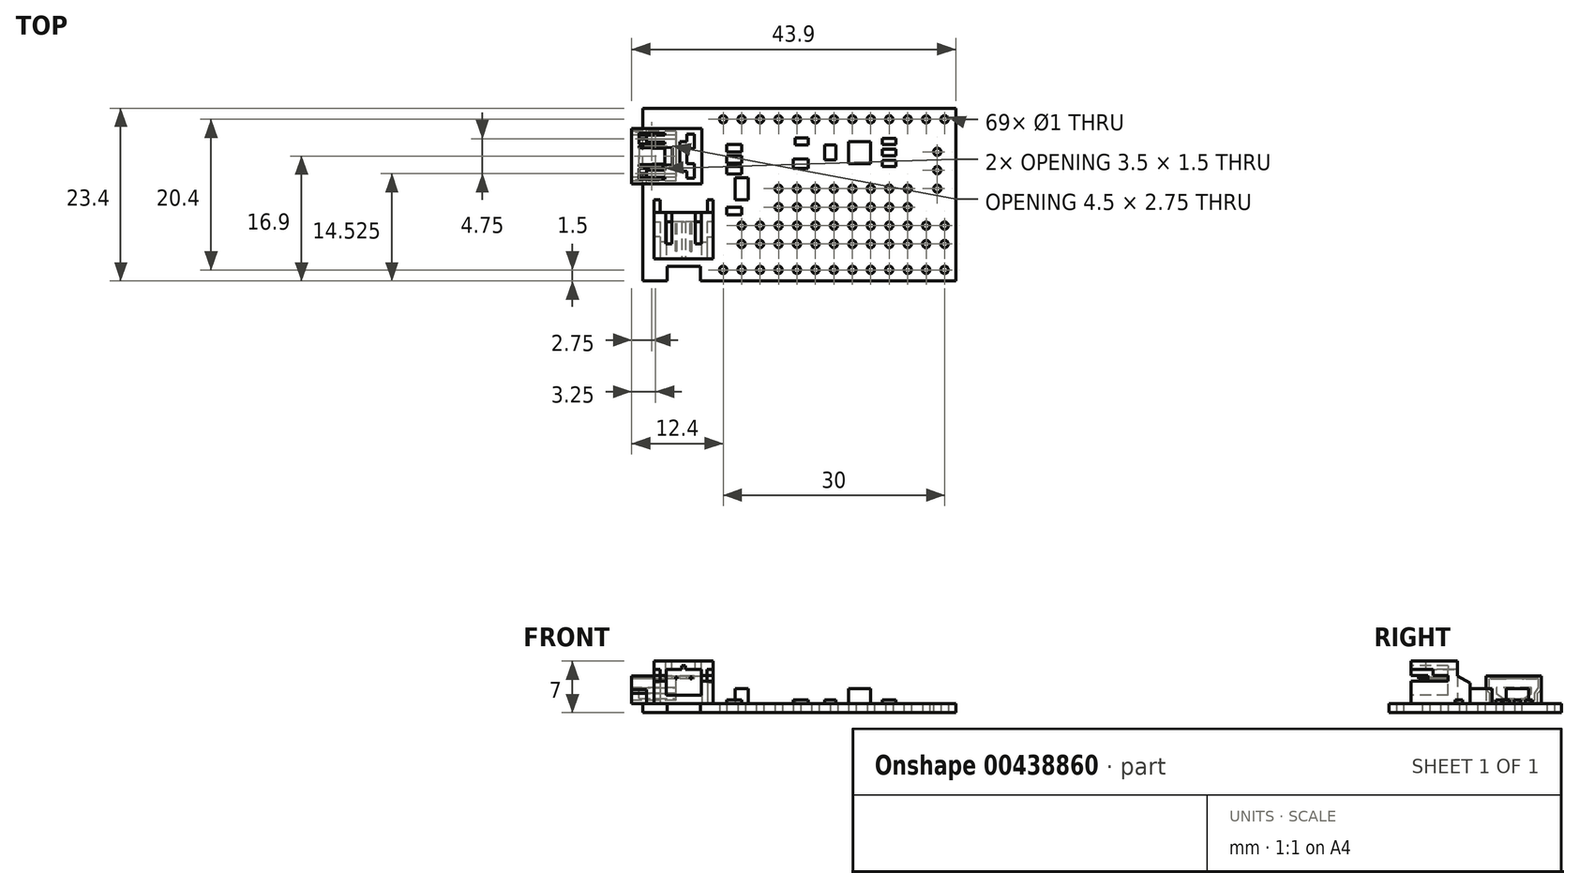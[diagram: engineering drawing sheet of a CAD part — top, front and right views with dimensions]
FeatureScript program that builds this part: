
annotation { "Feature Type Name" : "Feature", "Feature Type Description" : "" }
export const myFeature = defineFeature(function(context is Context, id is Id, definition is map)
    precondition{}
    {
        {
            var Q0;
            Q0=qCreatedBy(makeId("Top.planeOp"),FACE);
            var sketch = newSketch(context, id + "F0", { "sketchPlane" : qUnion([Q0])});
            skLineSegment(sketch, "E0.bottom", {"start": v(21.2, -11.7) * mm, "end": v(-21.2, -11.7) * mm});
            skLineSegment(sketch, "E0.top", {"start": v(21.2, 11.7) * mm, "end": v(-21.2, 11.7) * mm});
            skLineSegment(sketch, "E0.left", {"start": v(21.2, -11.7) * mm, "end": v(21.2, 11.7) * mm});
            skLineSegment(sketch, "E0.right", {"start": v(-21.2, -11.7) * mm, "end": v(-21.2, 11.7) * mm});
            skPoint(sketch, "E0.middle", {"position": v(0, 0) * mm});
            skLineSegment(sketch, "E1.bottom", {"start": v(-17.9, -11.7) * mm, "end": v(-13.4, -11.7) * mm, "construction": true});
            skLineSegment(sketch, "E1.top", {"start": v(-17.9, -9.7) * mm, "end": v(-13.4, -9.7) * mm});
            skLineSegment(sketch, "E1.left", {"start": v(-17.9, -11.7) * mm, "end": v(-17.9, -9.7) * mm});
            skLineSegment(sketch, "E1.right", {"start": v(-13.4, -11.7) * mm, "end": v(-13.4, -9.7) * mm});
            skCircle(sketch, "E2", {"center": v(19.7, -10.2) * mm, "radius": 0.5 * mm});
            skCircle(sketch, "E3.1.0.0", {"center": v(17.2, -10.2) * mm, "radius": 0.5 * mm});
            skCircle(sketch, "E3.2.0.0", {"center": v(14.7, -10.2) * mm, "radius": 0.5 * mm});
            skCircle(sketch, "E3.3.0.0", {"center": v(12.2, -10.2) * mm, "radius": 0.5 * mm});
            skCircle(sketch, "E3.4.0.0", {"center": v(9.7, -10.2) * mm, "radius": 0.5 * mm});
            skCircle(sketch, "E3.5.0.0", {"center": v(7.2, -10.2) * mm, "radius": 0.5 * mm});
            skCircle(sketch, "E3.6.0.0", {"center": v(4.7, -10.2) * mm, "radius": 0.5 * mm});
            skCircle(sketch, "E3.7.0.0", {"center": v(2.2, -10.2) * mm, "radius": 0.5 * mm});
            skCircle(sketch, "E3.8.0.0", {"center": v(-0.3, -10.2) * mm, "radius": 0.5 * mm});
            skCircle(sketch, "E3.9.0.0", {"center": v(-2.8, -10.2) * mm, "radius": 0.5 * mm});
            skCircle(sketch, "E3.10.0.0", {"center": v(-5.3, -10.2) * mm, "radius": 0.5 * mm});
            skCircle(sketch, "E3.11.0.0", {"center": v(-7.8, -10.2) * mm, "radius": 0.5 * mm});
            skCircle(sketch, "E3.12.0.0", {"center": v(-10.3, -10.2) * mm, "radius": 0.5 * mm});
            skLineSegment(sketch, "E3.direction1", {"start": v(19.7, -10.2) * mm, "end": v(17.2, -10.2) * mm, "construction": true});
            skCircle(sketch, "E4.0.1.0", {"center": v(-5.3, -6.7) * mm, "radius": 0.5 * mm});
            skCircle(sketch, "E4.0.1.1", {"center": v(-0.3, -6.7) * mm, "radius": 0.5 * mm});
            skCircle(sketch, "E4.0.1.2", {"center": v(17.2, -6.7) * mm, "radius": 0.5 * mm});
            skCircle(sketch, "E4.0.1.3", {"center": v(14.7, -6.7) * mm, "radius": 0.5 * mm});
            skCircle(sketch, "E4.0.1.4", {"center": v(12.2, -6.7) * mm, "radius": 0.5 * mm});
            skCircle(sketch, "E4.0.1.5", {"center": v(9.7, -6.7) * mm, "radius": 0.5 * mm});
            skCircle(sketch, "E4.0.1.6", {"center": v(19.7, -6.7) * mm, "radius": 0.5 * mm});
            skCircle(sketch, "E4.0.1.7", {"center": v(2.2, -6.7) * mm, "radius": 0.5 * mm});
            skCircle(sketch, "E4.0.1.8", {"center": v(4.7, -6.7) * mm, "radius": 0.5 * mm});
            skCircle(sketch, "E4.0.1.9", {"center": v(7.2, -6.7) * mm, "radius": 0.5 * mm});
            skCircle(sketch, "E4.0.1.10", {"center": v(-2.8, -6.7) * mm, "radius": 0.5 * mm});
            skCircle(sketch, "E4.0.1.12", {"center": v(-7.8, -6.7) * mm, "radius": 0.5 * mm});
            skLineSegment(sketch, "E4.direction1", {"start": v(-7.8, -10.2) * mm, "end": v(17.6, -10.2) * mm, "construction": true});
            skLineSegment(sketch, "E4.direction2", {"start": v(-7.8, -10.2) * mm, "end": v(-7.8, -6.7) * mm, "construction": true});
            skLineSegment(sketch, "E5.direction1", {"start": v(-7.8, -6.7) * mm, "end": v(17.6, -6.7) * mm, "construction": true});
            skLineSegment(sketch, "E5.direction2", {"start": v(-7.8, -6.7) * mm, "end": v(-7.8, -4.85) * mm, "construction": true});
            skPoint(sketch, "E6", {"position": v(-7.8, -8.45) * mm});
            skCircle(sketch, "E7.0.1.0", {"center": v(2.2, -4.2) * mm, "radius": 0.5 * mm});
            skCircle(sketch, "E7.0.1.1", {"center": v(9.7, -4.2) * mm, "radius": 0.5 * mm});
            skCircle(sketch, "E7.0.1.2", {"center": v(-5.3, -4.2) * mm, "radius": 0.5 * mm});
            skCircle(sketch, "E7.0.1.3", {"center": v(17.2, -4.2) * mm, "radius": 0.5 * mm});
            skCircle(sketch, "E7.0.1.4", {"center": v(-2.8, -4.2) * mm, "radius": 0.5 * mm});
            skCircle(sketch, "E7.0.1.5", {"center": v(-0.3, -4.2) * mm, "radius": 0.5 * mm});
            skCircle(sketch, "E7.0.1.6", {"center": v(14.7, -4.2) * mm, "radius": 0.5 * mm});
            skCircle(sketch, "E7.0.1.7", {"center": v(4.7, -4.2) * mm, "radius": 0.5 * mm});
            skCircle(sketch, "E7.0.1.8", {"center": v(7.2, -4.2) * mm, "radius": 0.5 * mm});
            skCircle(sketch, "E7.0.1.10", {"center": v(12.2, -4.2) * mm, "radius": 0.5 * mm});
            skCircle(sketch, "E7.0.1.11", {"center": v(19.7, -4.2) * mm, "radius": 0.5 * mm});
            skCircle(sketch, "E7.0.1.12", {"center": v(-7.8, -4.2) * mm, "radius": 0.5 * mm});
            skCircle(sketch, "E7.0.2.0", {"center": v(2.2, -1.7) * mm, "radius": 0.5 * mm});
            skCircle(sketch, "E7.0.2.1", {"center": v(9.7, -1.7) * mm, "radius": 0.5 * mm});
            skCircle(sketch, "E7.0.2.4", {"center": v(-2.8, -1.7) * mm, "radius": 0.5 * mm});
            skCircle(sketch, "E7.0.2.5", {"center": v(-0.3, -1.7) * mm, "radius": 0.5 * mm});
            skCircle(sketch, "E7.0.2.6", {"center": v(14.7, -1.7) * mm, "radius": 0.5 * mm});
            skCircle(sketch, "E7.0.2.7", {"center": v(4.7, -1.7) * mm, "radius": 0.5 * mm});
            skCircle(sketch, "E7.0.2.8", {"center": v(7.2, -1.7) * mm, "radius": 0.5 * mm});
            skCircle(sketch, "E7.0.2.10", {"center": v(12.2, -1.7) * mm, "radius": 0.5 * mm});
            skCircle(sketch, "E7.0.3.0", {"center": v(2.2, 0.8) * mm, "radius": 0.5 * mm});
            skCircle(sketch, "E7.0.3.1", {"center": v(9.7, 0.8) * mm, "radius": 0.5 * mm});
            skCircle(sketch, "E7.0.3.4", {"center": v(-2.8, 0.8) * mm, "radius": 0.5 * mm});
            skCircle(sketch, "E7.0.3.5", {"center": v(-0.3, 0.8) * mm, "radius": 0.5 * mm});
            skCircle(sketch, "E7.0.3.6", {"center": v(14.7, 0.8) * mm, "radius": 0.5 * mm});
            skCircle(sketch, "E7.0.3.7", {"center": v(4.7, 0.8) * mm, "radius": 0.5 * mm});
            skCircle(sketch, "E7.0.3.8", {"center": v(7.2, 0.8) * mm, "radius": 0.5 * mm});
            skCircle(sketch, "E7.0.3.10", {"center": v(12.2, 0.8) * mm, "radius": 0.5 * mm});
            skLineSegment(sketch, "E7.direction2", {"start": v(-7.8, -6.7) * mm, "end": v(-7.8, -4.2) * mm, "construction": true});
            skCircle(sketch, "E8", {"center": v(19.7, 10.2) * mm, "radius": 0.5 * mm});
            skCircle(sketch, "E9.1.0.0", {"center": v(17.2, 10.2) * mm, "radius": 0.5 * mm});
            skCircle(sketch, "E9.2.0.0", {"center": v(14.7, 10.2) * mm, "radius": 0.5 * mm});
            skCircle(sketch, "E9.3.0.0", {"center": v(12.2, 10.2) * mm, "radius": 0.5 * mm});
            skCircle(sketch, "E9.4.0.0", {"center": v(9.7, 10.2) * mm, "radius": 0.5 * mm});
            skCircle(sketch, "E9.5.0.0", {"center": v(7.2, 10.2) * mm, "radius": 0.5 * mm});
            skCircle(sketch, "E9.6.0.0", {"center": v(4.7, 10.2) * mm, "radius": 0.5 * mm});
            skCircle(sketch, "E9.7.0.0", {"center": v(2.2, 10.2) * mm, "radius": 0.5 * mm});
            skCircle(sketch, "E9.8.0.0", {"center": v(-0.3, 10.2) * mm, "radius": 0.5 * mm});
            skCircle(sketch, "E9.9.0.0", {"center": v(-2.8, 10.2) * mm, "radius": 0.5 * mm});
            skCircle(sketch, "E9.10.0.0", {"center": v(-5.3, 10.2) * mm, "radius": 0.5 * mm});
            skCircle(sketch, "E9.11.0.0", {"center": v(-7.8, 10.2) * mm, "radius": 0.5 * mm});
            skCircle(sketch, "E9.12.0.0", {"center": v(-10.3, 10.2) * mm, "radius": 0.5 * mm});
            skLineSegment(sketch, "E9.direction1", {"start": v(19.7, 10.2) * mm, "end": v(17.2, 10.2) * mm, "construction": true});
            skCircle(sketch, "E10", {"center": v(18.7, 0.8) * mm, "radius": 0.5 * mm});
            skCircle(sketch, "E11.0.1.0", {"center": v(18.7, 3.3) * mm, "radius": 0.5 * mm});
            skCircle(sketch, "E11.0.2.0", {"center": v(18.7, 5.8) * mm, "radius": 0.5 * mm});
            skLineSegment(sketch, "E11.direction1", {"start": v(18.7, 0.8) * mm, "end": v(43.86, 0.8) * mm, "construction": true});
            skLineSegment(sketch, "E11.direction2", {"start": v(18.7, 0.8) * mm, "end": v(18.7, 3.3) * mm, "construction": true});
            skSolve(sketch);
        }
        {
            var Q0;
            Q0=makeQuery(id+"F0.imprint","IMPRINT",FACE,{"disambiguationData":[TD([[makeQuery(id+"F0.imprint","IMPRINT",EDGE,{"derivedFrom":sQuery(id+"F0.wireOp",EDGE,"E0.top")}),1.0]])]});
            extrude(context, id + "F1", {"entities" : qUnion([Q0]), "depth" : 1.25 * mm});
        }
        {
            var Q0;
            Q0=makeQuery(id+"F1.opExtrude","CAP_FACE",FACE,{"disambiguationData":[OSD([sQuery(id+"F0.wireOp",EDGE,"E0.bottom"),sQuery(id+"F0.wireOp",EDGE,"E0.top"),sQuery(id+"F0.wireOp",EDGE,"E0.left"),sQuery(id+"F0.wireOp",EDGE,"E0.right"),sQuery(id+"F0.wireOp",EDGE,"E1.top"),sQuery(id+"F0.wireOp",EDGE,"E1.left"),sQuery(id+"F0.wireOp",EDGE,"E1.right"),sQuery(id+"F0.wireOp",EDGE,"E2"),sQuery(id+"F0.wireOp",EDGE,"E3.1.0.0"),sQuery(id+"F0.wireOp",EDGE,"E3.2.0.0"),sQuery(id+"F0.wireOp",EDGE,"E3.3.0.0"),sQuery(id+"F0.wireOp",EDGE,"E3.4.0.0"),sQuery(id+"F0.wireOp",EDGE,"E3.5.0.0"),sQuery(id+"F0.wireOp",EDGE,"E3.6.0.0"),sQuery(id+"F0.wireOp",EDGE,"E3.7.0.0"),sQuery(id+"F0.wireOp",EDGE,"E3.8.0.0"),sQuery(id+"F0.wireOp",EDGE,"E3.9.0.0"),sQuery(id+"F0.wireOp",EDGE,"E3.10.0.0"),sQuery(id+"F0.wireOp",EDGE,"E3.11.0.0"),sQuery(id+"F0.wireOp",EDGE,"E3.12.0.0"),sQuery(id+"F0.wireOp",EDGE,"E4.0.1.0"),sQuery(id+"F0.wireOp",EDGE,"E4.0.1.1"),sQuery(id+"F0.wireOp",EDGE,"E4.0.1.2"),sQuery(id+"F0.wireOp",EDGE,"E4.0.1.3"),sQuery(id+"F0.wireOp",EDGE,"E4.0.1.4"),sQuery(id+"F0.wireOp",EDGE,"E4.0.1.5"),sQuery(id+"F0.wireOp",EDGE,"E4.0.1.6"),sQuery(id+"F0.wireOp",EDGE,"E4.0.1.7"),sQuery(id+"F0.wireOp",EDGE,"E4.0.1.8"),sQuery(id+"F0.wireOp",EDGE,"E4.0.1.9"),sQuery(id+"F0.wireOp",EDGE,"E4.0.1.10"),sQuery(id+"F0.wireOp",EDGE,"E4.0.1.12"),sQuery(id+"F0.wireOp",EDGE,"E7.0.1.0"),sQuery(id+"F0.wireOp",EDGE,"E7.0.1.1"),sQuery(id+"F0.wireOp",EDGE,"E7.0.1.2"),sQuery(id+"F0.wireOp",EDGE,"E7.0.1.3"),sQuery(id+"F0.wireOp",EDGE,"E7.0.1.4"),sQuery(id+"F0.wireOp",EDGE,"E7.0.1.5"),sQuery(id+"F0.wireOp",EDGE,"E7.0.1.6"),sQuery(id+"F0.wireOp",EDGE,"E7.0.1.7"),sQuery(id+"F0.wireOp",EDGE,"E7.0.1.8"),sQuery(id+"F0.wireOp",EDGE,"E7.0.1.10"),sQuery(id+"F0.wireOp",EDGE,"E7.0.1.11"),sQuery(id+"F0.wireOp",EDGE,"E7.0.1.12"),sQuery(id+"F0.wireOp",EDGE,"E7.0.2.0"),sQuery(id+"F0.wireOp",EDGE,"E7.0.2.1"),sQuery(id+"F0.wireOp",EDGE,"E7.0.2.4"),sQuery(id+"F0.wireOp",EDGE,"E7.0.2.5"),sQuery(id+"F0.wireOp",EDGE,"E7.0.2.6"),sQuery(id+"F0.wireOp",EDGE,"E7.0.2.7"),sQuery(id+"F0.wireOp",EDGE,"E7.0.2.8"),sQuery(id+"F0.wireOp",EDGE,"E7.0.2.10"),sQuery(id+"F0.wireOp",EDGE,"E7.0.3.0"),sQuery(id+"F0.wireOp",EDGE,"E7.0.3.1"),sQuery(id+"F0.wireOp",EDGE,"E7.0.3.4"),sQuery(id+"F0.wireOp",EDGE,"E7.0.3.5"),sQuery(id+"F0.wireOp",EDGE,"E7.0.3.6"),sQuery(id+"F0.wireOp",EDGE,"E7.0.3.7"),sQuery(id+"F0.wireOp",EDGE,"E7.0.3.8"),sQuery(id+"F0.wireOp",EDGE,"E7.0.3.10"),sQuery(id+"F0.wireOp",EDGE,"E8"),sQuery(id+"F0.wireOp",EDGE,"E9.1.0.0"),sQuery(id+"F0.wireOp",EDGE,"E9.2.0.0"),sQuery(id+"F0.wireOp",EDGE,"E9.3.0.0"),sQuery(id+"F0.wireOp",EDGE,"E9.4.0.0"),sQuery(id+"F0.wireOp",EDGE,"E9.5.0.0"),sQuery(id+"F0.wireOp",EDGE,"E9.6.0.0"),sQuery(id+"F0.wireOp",EDGE,"E9.7.0.0"),sQuery(id+"F0.wireOp",EDGE,"E9.8.0.0"),sQuery(id+"F0.wireOp",EDGE,"E9.9.0.0"),sQuery(id+"F0.wireOp",EDGE,"E9.10.0.0"),sQuery(id+"F0.wireOp",EDGE,"E9.11.0.0"),sQuery(id+"F0.wireOp",EDGE,"E9.12.0.0"),sQuery(id+"F0.wireOp",EDGE,"E10"),sQuery(id+"F0.wireOp",EDGE,"E11.0.1.0"),sQuery(id+"F0.wireOp",EDGE,"E11.0.2.0")])],"isStart":false});
            var sketch = newSketch(context, id + "F2", { "sketchPlane" : qUnion([Q0])});
            skCircle(sketch, "E12", {"center": v(12.2, 10.2) * mm, "radius": 0.5 * mm});
            skCircle(sketch, "E13", {"center": v(-7.8, 10.2) * mm, "radius": 0.5 * mm});
            skCircle(sketch, "E14", {"center": v(-2.8, 0.8) * mm, "radius": 0.5 * mm});
            skSolve(sketch);
        }
        {
            var Q0;
            Q0=makeQuery(id+"F1.opExtrude","CAP_FACE",FACE,{"disambiguationData":[OSD([sQuery(id+"F0.wireOp",EDGE,"E0.bottom"),sQuery(id+"F0.wireOp",EDGE,"E0.top"),sQuery(id+"F0.wireOp",EDGE,"E0.left"),sQuery(id+"F0.wireOp",EDGE,"E0.right"),sQuery(id+"F0.wireOp",EDGE,"E1.top"),sQuery(id+"F0.wireOp",EDGE,"E1.left"),sQuery(id+"F0.wireOp",EDGE,"E1.right"),sQuery(id+"F0.wireOp",EDGE,"E2"),sQuery(id+"F0.wireOp",EDGE,"E3.1.0.0"),sQuery(id+"F0.wireOp",EDGE,"E3.2.0.0"),sQuery(id+"F0.wireOp",EDGE,"E3.3.0.0"),sQuery(id+"F0.wireOp",EDGE,"E3.4.0.0"),sQuery(id+"F0.wireOp",EDGE,"E3.5.0.0"),sQuery(id+"F0.wireOp",EDGE,"E3.6.0.0"),sQuery(id+"F0.wireOp",EDGE,"E3.7.0.0"),sQuery(id+"F0.wireOp",EDGE,"E3.8.0.0"),sQuery(id+"F0.wireOp",EDGE,"E3.9.0.0"),sQuery(id+"F0.wireOp",EDGE,"E3.10.0.0"),sQuery(id+"F0.wireOp",EDGE,"E3.11.0.0"),sQuery(id+"F0.wireOp",EDGE,"E3.12.0.0"),sQuery(id+"F0.wireOp",EDGE,"E4.0.1.0"),sQuery(id+"F0.wireOp",EDGE,"E4.0.1.1"),sQuery(id+"F0.wireOp",EDGE,"E4.0.1.2"),sQuery(id+"F0.wireOp",EDGE,"E4.0.1.3"),sQuery(id+"F0.wireOp",EDGE,"E4.0.1.4"),sQuery(id+"F0.wireOp",EDGE,"E4.0.1.5"),sQuery(id+"F0.wireOp",EDGE,"E4.0.1.6"),sQuery(id+"F0.wireOp",EDGE,"E4.0.1.7"),sQuery(id+"F0.wireOp",EDGE,"E4.0.1.8"),sQuery(id+"F0.wireOp",EDGE,"E4.0.1.9"),sQuery(id+"F0.wireOp",EDGE,"E4.0.1.10"),sQuery(id+"F0.wireOp",EDGE,"E4.0.1.12"),sQuery(id+"F0.wireOp",EDGE,"E7.0.1.0"),sQuery(id+"F0.wireOp",EDGE,"E7.0.1.1"),sQuery(id+"F0.wireOp",EDGE,"E7.0.1.2"),sQuery(id+"F0.wireOp",EDGE,"E7.0.1.3"),sQuery(id+"F0.wireOp",EDGE,"E7.0.1.4"),sQuery(id+"F0.wireOp",EDGE,"E7.0.1.5"),sQuery(id+"F0.wireOp",EDGE,"E7.0.1.6"),sQuery(id+"F0.wireOp",EDGE,"E7.0.1.7"),sQuery(id+"F0.wireOp",EDGE,"E7.0.1.8"),sQuery(id+"F0.wireOp",EDGE,"E7.0.1.10"),sQuery(id+"F0.wireOp",EDGE,"E7.0.1.11"),sQuery(id+"F0.wireOp",EDGE,"E7.0.1.12"),sQuery(id+"F0.wireOp",EDGE,"E7.0.2.0"),sQuery(id+"F0.wireOp",EDGE,"E7.0.2.1"),sQuery(id+"F0.wireOp",EDGE,"E7.0.2.4"),sQuery(id+"F0.wireOp",EDGE,"E7.0.2.5"),sQuery(id+"F0.wireOp",EDGE,"E7.0.2.6"),sQuery(id+"F0.wireOp",EDGE,"E7.0.2.7"),sQuery(id+"F0.wireOp",EDGE,"E7.0.2.8"),sQuery(id+"F0.wireOp",EDGE,"E7.0.2.10"),sQuery(id+"F0.wireOp",EDGE,"E7.0.3.0"),sQuery(id+"F0.wireOp",EDGE,"E7.0.3.1"),sQuery(id+"F0.wireOp",EDGE,"E7.0.3.4"),sQuery(id+"F0.wireOp",EDGE,"E7.0.3.5"),sQuery(id+"F0.wireOp",EDGE,"E7.0.3.6"),sQuery(id+"F0.wireOp",EDGE,"E7.0.3.7"),sQuery(id+"F0.wireOp",EDGE,"E7.0.3.8"),sQuery(id+"F0.wireOp",EDGE,"E7.0.3.10"),sQuery(id+"F0.wireOp",EDGE,"E8"),sQuery(id+"F0.wireOp",EDGE,"E9.1.0.0"),sQuery(id+"F0.wireOp",EDGE,"E9.2.0.0"),sQuery(id+"F0.wireOp",EDGE,"E9.3.0.0"),sQuery(id+"F0.wireOp",EDGE,"E9.4.0.0"),sQuery(id+"F0.wireOp",EDGE,"E9.5.0.0"),sQuery(id+"F0.wireOp",EDGE,"E9.6.0.0"),sQuery(id+"F0.wireOp",EDGE,"E9.7.0.0"),sQuery(id+"F0.wireOp",EDGE,"E9.8.0.0"),sQuery(id+"F0.wireOp",EDGE,"E9.9.0.0"),sQuery(id+"F0.wireOp",EDGE,"E9.10.0.0"),sQuery(id+"F0.wireOp",EDGE,"E9.11.0.0"),sQuery(id+"F0.wireOp",EDGE,"E9.12.0.0"),sQuery(id+"F0.wireOp",EDGE,"E10"),sQuery(id+"F0.wireOp",EDGE,"E11.0.1.0"),sQuery(id+"F0.wireOp",EDGE,"E11.0.2.0")])],"isStart":false});
            var sketch = newSketch(context, id + "F3", { "sketchPlane" : qUnion([Q0])});
            skLineSegment(sketch, "E15.bottom", {"start": v(13.13, 3.77) * mm, "end": v(11.28, 3.77) * mm});
            skLineSegment(sketch, "E15.top", {"start": v(13.13, 4.62) * mm, "end": v(11.28, 4.62) * mm});
            skLineSegment(sketch, "E15.left", {"start": v(13.13, 3.77) * mm, "end": v(13.12, 4.62) * mm});
            skLineSegment(sketch, "E15.right", {"start": v(11.28, 3.77) * mm, "end": v(11.28, 4.62) * mm});
            skPoint(sketch, "E15.middle", {"position": v(12.2, 4.2) * mm});
            skPoint(sketch, "E16.0.1.0", {"position": v(12.2, 5.7) * mm});
            skLineSegment(sketch, "E16.0.1.1", {"start": v(13.12, 5.27) * mm, "end": v(11.28, 5.27) * mm});
            skLineSegment(sketch, "E16.0.1.2", {"start": v(13.12, 6.12) * mm, "end": v(11.28, 6.12) * mm});
            skLineSegment(sketch, "E16.0.1.3", {"start": v(13.12, 5.27) * mm, "end": v(13.12, 6.12) * mm});
            skLineSegment(sketch, "E16.0.1.4", {"start": v(11.27, 5.27) * mm, "end": v(11.27, 6.12) * mm});
            skPoint(sketch, "E16.0.2.0", {"position": v(12.2, 7.2) * mm});
            skLineSegment(sketch, "E16.0.2.1", {"start": v(13.13, 6.77) * mm, "end": v(11.28, 6.77) * mm});
            skLineSegment(sketch, "E16.0.2.2", {"start": v(13.13, 7.62) * mm, "end": v(11.28, 7.62) * mm});
            skLineSegment(sketch, "E16.0.2.3", {"start": v(13.12, 6.77) * mm, "end": v(13.12, 7.62) * mm});
            skLineSegment(sketch, "E16.0.2.4", {"start": v(11.27, 6.77) * mm, "end": v(11.27, 7.62) * mm});
            skLineSegment(sketch, "E16.direction1", {"start": v(11.28, 3.77) * mm, "end": v(37.64, 3.77) * mm, "construction": true});
            skLineSegment(sketch, "E16.direction2", {"start": v(11.28, 3.77) * mm, "end": v(11.28, 5.27) * mm, "construction": true});
            skSolve(sketch);
        }
        {
            var Q0;
            Q0=makeQuery(id+"F2.imprint","IMPRINT",FACE,{"disambiguationData":[TD([[makeQuery(id+"F2.imprint","IMPRINT",EDGE,{"derivedFrom":sQuery(id+"F2.wireOp",EDGE,"E12")}),-1.0]])]});
            var sketch = newSketch(context, id + "F4", { "sketchPlane" : qUnion([Q0])});
            skLineSegment(sketch, "E17.bottom", {"start": v(9.7, 4.2) * mm, "end": v(6.7, 4.2) * mm});
            skLineSegment(sketch, "E17.top", {"start": v(9.7, 7.2) * mm, "end": v(6.7, 7.2) * mm});
            skLineSegment(sketch, "E17.left", {"start": v(9.7, 4.2) * mm, "end": v(9.7, 7.2) * mm});
            skLineSegment(sketch, "E17.right", {"start": v(6.7, 4.2) * mm, "end": v(6.7, 7.2) * mm});
            skPoint(sketch, "E17.middle", {"position": v(8.2, 5.7) * mm});
            skSolve(sketch);
        }
        {
            var Q0;
            Q0=makeQuery(id+"F2.imprint","IMPRINT",FACE,{"disambiguationData":[TD([[makeQuery(id+"F2.imprint","IMPRINT",EDGE,{"derivedFrom":sQuery(id+"F2.wireOp",EDGE,"E12")}),-1.0]])]});
            var sketch = newSketch(context, id + "F5", { "sketchPlane" : qUnion([Q0])});
            skLineSegment(sketch, "E18.bottom", {"start": v(4.95, 4.7) * mm, "end": v(3.45, 4.7) * mm});
            skLineSegment(sketch, "E18.top", {"start": v(4.95, 6.7) * mm, "end": v(3.45, 6.7) * mm});
            skLineSegment(sketch, "E18.left", {"start": v(4.95, 4.7) * mm, "end": v(4.95, 6.7) * mm});
            skLineSegment(sketch, "E18.right", {"start": v(3.45, 4.7) * mm, "end": v(3.45, 6.7) * mm});
            skPoint(sketch, "E18.middle", {"position": v(4.2, 5.7) * mm});
            skSolve(sketch);
        }
        {
            var Q0;
            Q0=makeQuery(id+"F2.imprint","IMPRINT",FACE,{"disambiguationData":[TD([[makeQuery(id+"F2.imprint","IMPRINT",EDGE,{"derivedFrom":sQuery(id+"F2.wireOp",EDGE,"E12")}),-1.0]])]});
            var sketch = newSketch(context, id + "F6", { "sketchPlane" : qUnion([Q0])});
            skLineSegment(sketch, "E19.bottom", {"start": v(1.2, 6.7) * mm, "end": v(-0.55, 6.7) * mm});
            skLineSegment(sketch, "E19.top", {"start": v(1.2, 7.7) * mm, "end": v(-0.55, 7.7) * mm});
            skLineSegment(sketch, "E19.left", {"start": v(1.2, 6.7) * mm, "end": v(1.2, 7.7) * mm});
            skLineSegment(sketch, "E19.right", {"start": v(-0.55, 6.7) * mm, "end": v(-0.55, 7.7) * mm});
            skPoint(sketch, "E19.middle", {"position": v(0.32, 7.2) * mm});
            skLineSegment(sketch, "E20.bottom", {"start": v(1.2, 3.57) * mm, "end": v(-0.8, 3.57) * mm});
            skLineSegment(sketch, "E20.top", {"start": v(1.2, 4.82) * mm, "end": v(-0.8, 4.82) * mm});
            skLineSegment(sketch, "E20.left", {"start": v(1.2, 3.57) * mm, "end": v(1.2, 4.82) * mm});
            skLineSegment(sketch, "E20.right", {"start": v(-0.8, 3.57) * mm, "end": v(-0.8, 4.82) * mm});
            skPoint(sketch, "E20.middle", {"position": v(0.2, 4.2) * mm});
            skSolve(sketch);
        }
        {
            var Q0;
            Q0=makeQuery(id+"F2.imprint","IMPRINT",FACE,{"disambiguationData":[TD([[makeQuery(id+"F2.imprint","IMPRINT",EDGE,{"derivedFrom":sQuery(id+"F2.wireOp",EDGE,"E12")}),-1.0]])]});
            var sketch = newSketch(context, id + "F7", { "sketchPlane" : qUnion([Q0])});
            skLineSegment(sketch, "E21.bottom", {"start": v(-7.8, 5.77) * mm, "end": v(-9.8, 5.77) * mm});
            skLineSegment(sketch, "E21.top", {"start": v(-7.8, 6.77) * mm, "end": v(-9.8, 6.77) * mm});
            skLineSegment(sketch, "E21.left", {"start": v(-7.8, 5.77) * mm, "end": v(-7.8, 6.77) * mm});
            skLineSegment(sketch, "E21.right", {"start": v(-9.8, 5.77) * mm, "end": v(-9.8, 6.77) * mm});
            skPoint(sketch, "E21.middle", {"position": v(-8.8, 6.27) * mm});
            skLineSegment(sketch, "E22.0.1.0", {"start": v(-7.8, 4.27) * mm, "end": v(-7.8, 5.27) * mm});
            skLineSegment(sketch, "E22.0.1.1", {"start": v(-9.8, 4.27) * mm, "end": v(-9.8, 5.27) * mm});
            skLineSegment(sketch, "E22.0.1.2", {"start": v(-7.8, 4.27) * mm, "end": v(-9.8, 4.27) * mm});
            skLineSegment(sketch, "E22.0.1.3", {"start": v(-7.8, 5.27) * mm, "end": v(-9.8, 5.27) * mm});
            skPoint(sketch, "E22.0.1.4", {"position": v(-8.8, 4.77) * mm});
            skLineSegment(sketch, "E22.0.2.0", {"start": v(-7.8, 2.77) * mm, "end": v(-7.8, 3.77) * mm});
            skLineSegment(sketch, "E22.0.2.1", {"start": v(-9.8, 2.77) * mm, "end": v(-9.8, 3.77) * mm});
            skLineSegment(sketch, "E22.0.2.2", {"start": v(-7.8, 2.77) * mm, "end": v(-9.8, 2.77) * mm});
            skLineSegment(sketch, "E22.0.2.3", {"start": v(-7.8, 3.77) * mm, "end": v(-9.8, 3.77) * mm});
            skPoint(sketch, "E22.0.2.4", {"position": v(-8.8, 3.27) * mm});
            skLineSegment(sketch, "E22.direction1", {"start": v(-9.8, 5.77) * mm, "end": v(16.86, 5.77) * mm, "construction": true});
            skLineSegment(sketch, "E22.direction2", {"start": v(-9.8, 5.77) * mm, "end": v(-9.8, 4.27) * mm, "construction": true});
            skLineSegment(sketch, "E23.direction1", {"start": v(-9.8, 2.77) * mm, "end": v(15.6, 2.77) * mm, "construction": true});
            skPoint(sketch, "E24.0.1.0", {"position": v(-8.8, -2.23) * mm});
            skLineSegment(sketch, "E24.0.1.1", {"start": v(-9.8, -2.73) * mm, "end": v(-9.8, -1.73) * mm});
            skLineSegment(sketch, "E24.0.1.2", {"start": v(-7.8, -2.73) * mm, "end": v(-7.8, -1.73) * mm});
            skLineSegment(sketch, "E24.0.1.3", {"start": v(-7.8, -1.73) * mm, "end": v(-9.8, -1.73) * mm});
            skLineSegment(sketch, "E24.0.1.4", {"start": v(-7.8, -2.73) * mm, "end": v(-9.8, -2.73) * mm});
            skLineSegment(sketch, "E24.direction2", {"start": v(-9.8, 2.77) * mm, "end": v(-9.8, -2.73) * mm, "construction": true});
            skSolve(sketch);
        }
        {
            var Q0;
            Q0=makeQuery(id+"F2.imprint","IMPRINT",FACE,{"disambiguationData":[TD([[makeQuery(id+"F2.imprint","IMPRINT",EDGE,{"derivedFrom":sQuery(id+"F2.wireOp",EDGE,"E12")}),-1.0]])]});
            var sketch = newSketch(context, id + "F8", { "sketchPlane" : qUnion([Q0])});
            skLineSegment(sketch, "E25.bottom", {"start": v(-6.93, -0.7) * mm, "end": v(-8.68, -0.7) * mm});
            skLineSegment(sketch, "E25.top", {"start": v(-6.93, 2.3) * mm, "end": v(-8.68, 2.3) * mm});
            skLineSegment(sketch, "E25.left", {"start": v(-6.93, -0.7) * mm, "end": v(-6.93, 2.3) * mm});
            skLineSegment(sketch, "E25.right", {"start": v(-8.68, -0.7) * mm, "end": v(-8.68, 2.3) * mm});
            skPoint(sketch, "E25.middle", {"position": v(-7.8, 0.8) * mm});
            skSolve(sketch);
        }
        {
            var Q0;
            Q0=qSketchRegion(id+"F3",true);
            extrude(context, id + "F9", {"entities" : qUnion([Q0]), "depth" : .5 * mm});
        }
        {
            var Q0;
            Q0=qSketchRegion(id+"F5",true);
            extrude(context, id + "F10", {"entities" : qUnion([Q0]), "depth" : .5 * mm});
        }
        {
            var Q0;
            Q0=qSketchRegion(id+"F6",true);
            extrude(context, id + "F11", {"entities" : qUnion([Q0]), "depth" : .5 * mm});
        }
        {
            var Q0;
            Q0=qSketchRegion(id+"F7",true);
            extrude(context, id + "F12", {"entities" : qUnion([Q0]), "depth" : .5 * mm});
        }
        {
            var Q0;
            Q0=qSketchRegion(id+"F4",true);
            extrude(context, id + "F13", {"entities" : qUnion([Q0]), "depth" : 2 * mm});
        }
        {
            var Q0;
            Q0=qSketchRegion(id+"F8",true);
            extrude(context, id + "F14", {"entities" : qUnion([Q0]), "depth" : 2 * mm});
        }
        {
            var Q0;
            Q0=makeQuery(id+"F2.imprint","IMPRINT",FACE,{"disambiguationData":[TD([[makeQuery(id+"F2.imprint","IMPRINT",EDGE,{"derivedFrom":sQuery(id+"F2.wireOp",EDGE,"E12")}),-1.0]])]});
            var sketch = newSketch(context, id + "F15", { "sketchPlane" : qUnion([Q0])});
            skLineSegment(sketch, "E26.bottom", {"start": v(-11.65, -8.7) * mm, "end": v(-19.65, -8.7) * mm});
            skLineSegment(sketch, "E26.top", {"start": v(-11.65, -0.7) * mm, "end": v(-19.65, -0.7) * mm});
            skLineSegment(sketch, "E26.left", {"start": v(-11.65, -8.7) * mm, "end": v(-11.65, -0.7) * mm});
            skLineSegment(sketch, "E26.right", {"start": v(-19.65, -8.7) * mm, "end": v(-19.65, -0.7) * mm});
            skPoint(sketch, "E26.middle", {"position": v(-15.65, -4.7) * mm});
            skLineSegment(sketch, "E27.bottom", {"start": v(-18.85, -0.7) * mm, "end": v(-12.45, -0.7) * mm});
            skLineSegment(sketch, "E27.top", {"start": v(-18.85, -2.45) * mm, "end": v(-12.45, -2.45) * mm});
            skLineSegment(sketch, "E27.left", {"start": v(-18.85, -0.7) * mm, "end": v(-18.85, -2.45) * mm});
            skLineSegment(sketch, "E27.right", {"start": v(-12.45, -0.7) * mm, "end": v(-12.45, -2.45) * mm});
            skPoint(sketch, "E28", {"position": v(-15.65, -2.45) * mm});
            skSolve(sketch);
        }
        {
            var Q0;
            Q0=makeQuery(id+"F15.imprint","IMPRINT",FACE,{"disambiguationData":[TD([[makeQuery(id+"F15.imprint","IMPRINT",EDGE,{"derivedFrom":sQuery(id+"F15.wireOp",EDGE,"E26.bottom")}),-1.0]])]});
            extrude(context, id + "F16", {"entities" : qUnion([Q0]), "depth" : 5.75 * mm});
        }
        {
            var Q0;
            Q0=makeQuery(id+"F2.imprint","IMPRINT",FACE,{"disambiguationData":[TD([[makeQuery(id+"F2.imprint","IMPRINT",EDGE,{"derivedFrom":sQuery(id+"F2.wireOp",EDGE,"E12")}),-1.0]])]});
            var sketch = newSketch(context, id + "F17", { "sketchPlane" : qUnion([Q0])});
            skLineSegment(sketch, "E29.bottom", {"start": v(-22.7, 1.45) * mm, "end": v(-13.2, 1.45) * mm});
            skLineSegment(sketch, "E29.top", {"start": v(-22.7, 8.95) * mm, "end": v(-13.2, 8.95) * mm});
            skLineSegment(sketch, "E29.left", {"start": v(-22.7, 1.45) * mm, "end": v(-22.7, 8.95) * mm});
            skLineSegment(sketch, "E29.right", {"start": v(-13.2, 1.45) * mm, "end": v(-13.2, 8.95) * mm});
            skPoint(sketch, "E29.middle", {"position": v(-17.95, 5.2) * mm});
            skSolve(sketch);
        }
        {
            var Q0;
            Q0=qSketchRegion(id+"F17",true);
            extrude(context, id + "F18", {"entities" : qUnion([Q0]), "depth" : 3.75 * mm});
        }
        {
            var Q0;
            Q0=makeQuery(id+"F16.opExtrude","SWEPT_FACE",FACE,{"disambiguationData":[OSD([sQuery(id+"F15.wireOp",EDGE,"E26.bottom")])]});
            var sketch = newSketch(context, id + "F19", { "sketchPlane" : qUnion([Q0])});
            skLineSegment(sketch, "E30.bottom", {"start": v(-13.28, 2.37) * mm, "end": v(-18.03, 2.37) * mm});
            skLineSegment(sketch, "E30.top", {"start": v(-13.28, 5.87) * mm, "end": v(-18.03, 5.87) * mm});
            skLineSegment(sketch, "E30.left", {"start": v(-13.28, 2.37) * mm, "end": v(-13.28, 5.87) * mm});
            skLineSegment(sketch, "E30.right", {"start": v(-18.03, 2.37) * mm, "end": v(-18.03, 5.88) * mm});
            skPoint(sketch, "E30.middle", {"position": v(-15.65, 4.12) * mm});
            skSolve(sketch);
        }
        {
            var Q0;
            Q0=makeQuery(id+"F19.imprint","IMPRINT",FACE,{"disambiguationData":[TD([[makeQuery(id+"F19.imprint","IMPRINT",EDGE,{"derivedFrom":sQuery(id+"F19.wireOp",EDGE,"E30.bottom")}),-1.0]])]});
            extrude(context, id + "F20", {"entities" : qUnion([Q0]), "operationType" : NewBodyOperationType.REMOVE, "oppositeDirection" : true, "depth" : 5 * mm});
        }
        {
            var Q0;
            Q0=makeQuery(id+"F18.opExtrude","SWEPT_FACE",FACE,{"disambiguationData":[OSD([sQuery(id+"F17.wireOp",EDGE,"E29.left")])]});
            var sketch = newSketch(context, id + "F21", { "sketchPlane" : qUnion([Q0])});
            skLineSegment(sketch, "E31.bottom", {"start": v(-1.95, 1.25) * mm, "end": v(-8.45, 1.25) * mm});
            skLineSegment(sketch, "E31.top", {"start": v(-1.95, 2.62) * mm, "end": v(-8.45, 2.62) * mm});
            skLineSegment(sketch, "E31.left", {"start": v(-1.95, 1.25) * mm, "end": v(-1.95, 2.62) * mm});
            skLineSegment(sketch, "E31.right", {"start": v(-8.45, 1.25) * mm, "end": v(-8.45, 2.62) * mm});
            skPoint(sketch, "E31.middle", {"position": v(-5.2, 1.94) * mm});
            skLineSegment(sketch, "E32", {"start": v(-8.45, 2.62) * mm, "end": v(-8.95, 3.13) * mm});
            skLineSegment(sketch, "E33", {"start": v(-1.45, 3.12) * mm, "end": v(-1.95, 2.62) * mm});
            skSolve(sketch);
        }
        {
            var Q0;
            {var subQ0=sQuery(id+"F21.wireOp",EDGE,"E31.right");Q0=makeQuery(id+"F21.imprint","IMPRINT",FACE,{"disambiguationData":[TD([[makeQuery(id+"F21.imprint","IMPRINT",EDGE,{"derivedFrom":subQ0}),1.0]])]});}
            var Q1;
            {var subQ0=sQuery(id+"F21.wireOp",EDGE,"E31.left");Q1=makeQuery(id+"F21.imprint","IMPRINT",FACE,{"disambiguationData":[TD([[makeQuery(id+"F21.imprint","IMPRINT",EDGE,{"derivedFrom":subQ0}),-1.0]])]});}
            extrude(context, id + "F22", {"entities" : qUnion([Q0, Q1]), "operationType" : NewBodyOperationType.REMOVE, "oppositeDirection" : true, "depth" : 2 * mm});
        }
        {
            var Q0;
            Q0=makeQuery(id+"F18.opExtrude","SWEPT_FACE",FACE,{"disambiguationData":[OSD([sQuery(id+"F17.wireOp",EDGE,"E29.left")])]});
            var sketch = newSketch(context, id + "F23", { "sketchPlane" : qUnion([Q0])});
            skLineSegment(sketch, "E34", {"start": v(-8.55, 4.6) * mm, "end": v(-1.85, 4.6) * mm});
            skLineSegment(sketch, "E35", {"start": v(-1.85, 4.6) * mm, "end": v(-1.85, 3.37) * mm});
            skLineSegment(sketch, "E36", {"start": v(-1.85, 3.37) * mm, "end": v(-2.35, 2.62) * mm});
            skLineSegment(sketch, "E37", {"start": v(-2.35, 2.62) * mm, "end": v(-2.35, 1.65) * mm});
            skLineSegment(sketch, "E38", {"start": v(-2.35, 1.65) * mm, "end": v(-8.05, 1.65) * mm});
            skLineSegment(sketch, "E39", {"start": v(-8.05, 1.65) * mm, "end": v(-8.05, 2.62) * mm});
            skLineSegment(sketch, "E40", {"start": v(-8.05, 2.62) * mm, "end": v(-8.55, 3.37) * mm});
            skLineSegment(sketch, "E41", {"start": v(-8.55, 3.37) * mm, "end": v(-8.55, 4.6) * mm});
            skPoint(sketch, "E42", {"position": v(-5.2, 4.6) * mm});
            skPoint(sketch, "E43", {"position": v(-5.2, 1.65) * mm});
            skSolve(sketch);
        }
        {
            var Q0;
            Q0=makeQuery(id+"F23.imprint","IMPRINT",FACE,{"disambiguationData":[TD([[makeQuery(id+"F23.imprint","IMPRINT",EDGE,{"derivedFrom":sQuery(id+"F23.wireOp",EDGE,"E34")}),-1.0]])]});
            extrude(context, id + "F24", {"entities" : qUnion([Q0]), "operationType" : NewBodyOperationType.REMOVE, "oppositeDirection" : true, "depth" : 6 * mm});
        }
        {
            var Q0;
            Q0=makeQuery(id+"F18.opExtrude","CAP_FACE",FACE,{"disambiguationData":[OSD([sQuery(id+"F17.wireOp",EDGE,"E29.bottom"),sQuery(id+"F17.wireOp",EDGE,"E29.top"),sQuery(id+"F17.wireOp",EDGE,"E29.left"),sQuery(id+"F17.wireOp",EDGE,"E29.right")])],"isStart":false});
            var sketch = newSketch(context, id + "F25", { "sketchPlane" : qUnion([Q0])});
            skLineSegment(sketch, "E44", {"start": v(-13.2, 5.2) * mm, "end": v(-22.7, 5.2) * mm, "construction": true});
            skLineSegment(sketch, "E45", {"start": v(-17.2, 5.2) * mm, "end": v(-17.2, 6.32) * mm});
            skLineSegment(sketch, "E46", {"start": v(-17.2, 6.32) * mm, "end": v(-21.7, 6.57) * mm});
            skLineSegment(sketch, "E47", {"start": v(-21.7, 6.57) * mm, "end": v(-21.7, 6.32) * mm});
            skLineSegment(sketch, "E48", {"start": v(-21.7, 6.32) * mm, "end": v(-18.2, 6.2) * mm});
            skLineSegment(sketch, "E49", {"start": v(-18.2, 6.2) * mm, "end": v(-18.2, 5.2) * mm});
            skLineSegment(sketch, "E50", {"start": v(-18.2, 8.32) * mm, "end": v(-21.7, 8.32) * mm});
            skLineSegment(sketch, "E51", {"start": v(-21.7, 8.32) * mm, "end": v(-21.7, 6.82) * mm});
            skLineSegment(sketch, "E52", {"start": v(-21.7, 6.82) * mm, "end": v(-18.2, 6.82) * mm});
            skLineSegment(sketch, "E53", {"start": v(-18.2, 6.82) * mm, "end": v(-18.2, 7.07) * mm});
            skLineSegment(sketch, "E54", {"start": v(-18.2, 7.07) * mm, "end": v(-20.7, 7.07) * mm});
            skLineSegment(sketch, "E55", {"start": v(-20.7, 7.07) * mm, "end": v(-20.7, 8.07) * mm});
            skLineSegment(sketch, "E56", {"start": v(-20.7, 8.07) * mm, "end": v(-18.2, 8.07) * mm});
            skLineSegment(sketch, "E57", {"start": v(-18.2, 8.07) * mm, "end": v(-18.2, 8.32) * mm});
            skLineSegment(sketch, "E58", {"start": v(-14.2, 8.2) * mm, "end": v(-14.2, 6.2) * mm});
            skLineSegment(sketch, "E59", {"start": v(-14.2, 6.2) * mm, "end": v(-15.2, 6.2) * mm});
            skLineSegment(sketch, "E60", {"start": v(-15.2, 6.2) * mm, "end": v(-15.2, 5.2) * mm});
            skLineSegment(sketch, "E61", {"start": v(-14.2, 8.2) * mm, "end": v(-15.2, 8.2) * mm});
            skLineSegment(sketch, "E62", {"start": v(-15.2, 8.2) * mm, "end": v(-15.2, 7.2) * mm});
            skLineSegment(sketch, "E63", {"start": v(-15.2, 7.2) * mm, "end": v(-16.2, 7.2) * mm});
            skLineSegment(sketch, "E64", {"start": v(-16.2, 7.2) * mm, "end": v(-16.2, 5.2) * mm});
            skLineSegment(sketch, "E65", {"start": v(-13.2, 8.2) * mm, "end": v(-13.45, 8.2) * mm});
            skLineSegment(sketch, "E66", {"start": v(-13.45, 8.2) * mm, "end": v(-13.45, 5.2) * mm});
            skLineSegment(sketch, "E67.MirrorCS", {"start": v(-21.7, 3.82) * mm, "end": v(-21.7, 4.07) * mm});
            skLineSegment(sketch, "E68.MirrorCS", {"start": v(-18.2, 2.32) * mm, "end": v(-18.2, 2.07) * mm});
            skLineSegment(sketch, "E69.MirrorCS", {"start": v(-18.2, 3.57) * mm, "end": v(-18.2, 3.32) * mm});
            skLineSegment(sketch, "E70.MirrorCS", {"start": v(-13.2, 2.2) * mm, "end": v(-13.45, 2.2) * mm});
            skLineSegment(sketch, "E71.MirrorCS", {"start": v(-17.2, 4.08) * mm, "end": v(-21.7, 3.82) * mm});
            skLineSegment(sketch, "E72.MirrorCS", {"start": v(-17.2, 5.2) * mm, "end": v(-17.2, 4.08) * mm});
            skLineSegment(sketch, "E73.MirrorCS", {"start": v(-21.7, 3.58) * mm, "end": v(-18.2, 3.58) * mm});
            skLineSegment(sketch, "E74.MirrorCS", {"start": v(-18.2, 4.2) * mm, "end": v(-18.2, 5.2) * mm});
            skLineSegment(sketch, "E75.MirrorCS", {"start": v(-14.2, 4.2) * mm, "end": v(-15.2, 4.2) * mm});
            skLineSegment(sketch, "E76.MirrorCS", {"start": v(-21.7, 4.08) * mm, "end": v(-18.2, 4.2) * mm});
            skLineSegment(sketch, "E77.MirrorCS", {"start": v(-14.2, 2.2) * mm, "end": v(-14.2, 4.2) * mm});
            skLineSegment(sketch, "E78.MirrorCS", {"start": v(-15.2, 4.2) * mm, "end": v(-15.2, 5.2) * mm});
            skLineSegment(sketch, "E79.MirrorCS", {"start": v(-15.2, 2.2) * mm, "end": v(-15.2, 3.2) * mm});
            skLineSegment(sketch, "E80.MirrorCS", {"start": v(-18.2, 2.08) * mm, "end": v(-21.7, 2.08) * mm});
            skLineSegment(sketch, "E81.MirrorCS", {"start": v(-20.7, 3.32) * mm, "end": v(-20.7, 2.32) * mm});
            skLineSegment(sketch, "E82.MirrorCS", {"start": v(-15.2, 3.2) * mm, "end": v(-16.2, 3.2) * mm});
            skLineSegment(sketch, "E83.MirrorCS", {"start": v(-21.7, 2.07) * mm, "end": v(-21.7, 3.57) * mm});
            skLineSegment(sketch, "E84.MirrorCS", {"start": v(-20.7, 2.32) * mm, "end": v(-18.2, 2.32) * mm});
            skLineSegment(sketch, "E85.MirrorCS", {"start": v(-18.2, 3.32) * mm, "end": v(-20.7, 3.32) * mm});
            skLineSegment(sketch, "E86.MirrorCS", {"start": v(-14.2, 2.2) * mm, "end": v(-15.2, 2.2) * mm});
            skLineSegment(sketch, "E87.MirrorCS", {"start": v(-16.2, 3.2) * mm, "end": v(-16.2, 5.2) * mm});
            skLineSegment(sketch, "E88.MirrorCS", {"start": v(-13.45, 2.2) * mm, "end": v(-13.45, 5.2) * mm});
            skSolve(sketch);
        }
        {
            var Q0;
            Q0=qSketchRegion(id+"F25",true);
            var Q1;
            Q1=makeQuery(id+"F24.boolean.opBoolean","COPY",FACE,{"derivedFrom":makeQuery(id+"F24.opExtrude","SWEPT_FACE",FACE,{"disambiguationData":[OSD([sQuery(id+"F23.wireOp",EDGE,"E34")])]})});
            extrude(context, id + "F26", {"entities" : qUnion([Q0]), "operationType" : NewBodyOperationType.REMOVE, "endBound" : BoundingType.UP_TO_SURFACE, "oppositeDirection" : true, "endBoundEntityFace" : qUnion([Q1]), "depth" : 25.4 * mm});
        }
        {
            var Q0;
            Q0=makeQuery(id+"F24.boolean.opBoolean","COPY",FACE,{"derivedFrom":makeQuery(id+"F24.opExtrude","CAP_FACE",FACE,{"disambiguationData":[OSD([sQuery(id+"F23.wireOp",EDGE,"E34"),sQuery(id+"F23.wireOp",EDGE,"E35"),sQuery(id+"F23.wireOp",EDGE,"E36"),sQuery(id+"F23.wireOp",EDGE,"E37"),sQuery(id+"F23.wireOp",EDGE,"E38"),sQuery(id+"F23.wireOp",EDGE,"E39"),sQuery(id+"F23.wireOp",EDGE,"E40"),sQuery(id+"F23.wireOp",EDGE,"E41")])],"isStart":false})});
            var sketch = newSketch(context, id + "F27", { "sketchPlane" : qUnion([Q0])});
            skLineSegment(sketch, "E89", {"start": v(-7.57, 3.4) * mm, "end": v(-2.82, 3.4) * mm});
            skLineSegment(sketch, "E90", {"start": v(-2.82, 3.4) * mm, "end": v(-2.82, 2.65) * mm});
            skLineSegment(sketch, "E91", {"start": v(-2.82, 2.65) * mm, "end": v(-3.82, 1.9) * mm});
            skLineSegment(sketch, "E92", {"start": v(-3.82, 1.9) * mm, "end": v(-6.57, 1.9) * mm});
            skLineSegment(sketch, "E93", {"start": v(-6.57, 1.9) * mm, "end": v(-7.57, 2.65) * mm});
            skLineSegment(sketch, "E94", {"start": v(-7.57, 2.65) * mm, "end": v(-7.57, 3.4) * mm});
            skPoint(sketch, "E95", {"position": v(-5.2, 3.4) * mm});
            skPoint(sketch, "E96", {"position": v(-5.2, 1.9) * mm});
            skSolve(sketch);
        }
        {
            var Q0;
            Q0=makeQuery(id+"F27.imprint","IMPRINT",FACE,{"disambiguationData":[TD([[makeQuery(id+"F27.imprint","IMPRINT",EDGE,{"derivedFrom":sQuery(id+"F27.wireOp",EDGE,"E89")}),-1.0]])]});
            extrude(context, id + "F28", {"entities" : qUnion([Q0]), "depth" : 5 * mm});
        }
        {
            var Q0;
            Q0=makeQuery(id+"F16.opExtrude","CAP_FACE",FACE,{"disambiguationData":[OSD([sQuery(id+"F15.wireOp",EDGE,"E26.bottom"),sQuery(id+"F15.wireOp",EDGE,"E26.top"),sQuery(id+"F15.wireOp",EDGE,"E26.left"),sQuery(id+"F15.wireOp",EDGE,"E26.right"),sQuery(id+"F15.wireOp",EDGE,"E27.top"),sQuery(id+"F15.wireOp",EDGE,"E27.left"),sQuery(id+"F15.wireOp",EDGE,"E27.right")])],"isStart":false});
            var sketch = newSketch(context, id + "F29", { "sketchPlane" : qUnion([Q0])});
            skLineSegment(sketch, "E97", {"start": v(-15.65, -2.45) * mm, "end": v(-15.65, -8.7) * mm, "construction": true});
            skLineSegment(sketch, "E98", {"start": v(-18.05, -2.45) * mm, "end": v(-18.05, -6.7) * mm});
            skLineSegment(sketch, "E99", {"start": v(-18.05, -6.7) * mm, "end": v(-17.25, -6.7) * mm});
            skLineSegment(sketch, "E100", {"start": v(-17.25, -6.7) * mm, "end": v(-17.25, -2.45) * mm});
            skLineSegment(sketch, "E101.MirrorCS", {"start": v(-13.25, -2.45) * mm, "end": v(-13.25, -6.7) * mm});
            skLineSegment(sketch, "E102.MirrorCS", {"start": v(-13.25, -6.7) * mm, "end": v(-14.05, -6.7) * mm});
            skLineSegment(sketch, "E103.MirrorCS", {"start": v(-14.05, -6.7) * mm, "end": v(-14.05, -2.45) * mm});
            skSolve(sketch);
        }
        {
            var Q0;
            {var subQ0=sQuery(id+"F29.wireOp",EDGE,"E98");Q0=makeQuery(id+"F29.imprint","IMPRINT",FACE,{"disambiguationData":[TD([[makeQuery(id+"F29.imprint","IMPRINT",EDGE,{"derivedFrom":subQ0}),1.0]])]});}
            var Q1;
            {var subQ0=sQuery(id+"F29.wireOp",EDGE,"E101.MirrorCS");Q1=makeQuery(id+"F29.imprint","IMPRINT",FACE,{"disambiguationData":[TD([[makeQuery(id+"F29.imprint","IMPRINT",EDGE,{"derivedFrom":subQ0}),-1.0]])]});}
            var Q2;
            Q2=makeQuery(id+"F20.boolean.opBoolean","COPY",FACE,{"derivedFrom":makeQuery(id+"F20.opExtrude","SWEPT_FACE",FACE,{"disambiguationData":[OSD([sQuery(id+"F19.wireOp",EDGE,"E30.top")])]})});
            extrude(context, id + "F30", {"entities" : qUnion([Q0, Q1]), "operationType" : NewBodyOperationType.REMOVE, "endBound" : BoundingType.UP_TO_SURFACE, "oppositeDirection" : true, "endBoundEntityFace" : qUnion([Q2]), "depth" : 25.4 * mm});
        }
        {
            var Q0;
            Q0=makeQuery(id+"F16.opExtrude","SWEPT_FACE",FACE,{"disambiguationData":[OSD([sQuery(id+"F15.wireOp",EDGE,"E26.bottom")])]});
            var sketch = newSketch(context, id + "F31", { "sketchPlane" : qUnion([Q0])});
            skLineSegment(sketch, "E104", {"start": v(-18.03, 5.06) * mm, "end": v(-19.65, 5.06) * mm});
            skLineSegment(sketch, "E105", {"start": v(-18.84, 5.06) * mm, "end": v(-18.84, 4.25) * mm});
            skLineSegment(sketch, "E106", {"start": v(-18.84, 4.25) * mm, "end": v(-18.03, 4.25) * mm});
            skLineSegment(sketch, "E107", {"start": v(-18.84, 4.25) * mm, "end": v(-19.65, 4.25) * mm});
            skLineSegment(sketch, "E108", {"start": v(-18.84, 5.06) * mm, "end": v(-18.84, 5.88) * mm});
            skLineSegment(sketch, "E109", {"start": v(-18.84, 5.88) * mm, "end": v(-19.65, 5.88) * mm});
            skLineSegment(sketch, "E110", {"start": v(-15.65, 7) * mm, "end": v(-15.65, 1.25) * mm, "construction": true});
            skLineSegment(sketch, "E111", {"start": v(-15.9, 5.87) * mm, "end": v(-15.9, 6.37) * mm});
            skLineSegment(sketch, "E112", {"start": v(-15.9, 6.37) * mm, "end": v(-15.65, 6.37) * mm});
            skLineSegment(sketch, "E113.MirrorCS", {"start": v(-15.4, 5.87) * mm, "end": v(-15.4, 6.37) * mm});
            skLineSegment(sketch, "E114.MirrorCS", {"start": v(-12.46, 5.06) * mm, "end": v(-12.46, 4.25) * mm});
            skLineSegment(sketch, "E115.MirrorCS", {"start": v(-13.27, 5.06) * mm, "end": v(-11.65, 5.06) * mm});
            skLineSegment(sketch, "E116.MirrorCS", {"start": v(-12.46, 4.25) * mm, "end": v(-11.65, 4.25) * mm});
            skLineSegment(sketch, "E117.MirrorCS", {"start": v(-15.4, 6.37) * mm, "end": v(-15.65, 6.37) * mm});
            skLineSegment(sketch, "E118.MirrorCS", {"start": v(-12.46, 5.88) * mm, "end": v(-11.65, 5.88) * mm});
            skLineSegment(sketch, "E119.MirrorCS", {"start": v(-12.46, 5.06) * mm, "end": v(-12.46, 5.88) * mm});
            skLineSegment(sketch, "E120.MirrorCS", {"start": v(-12.46, 4.25) * mm, "end": v(-13.27, 4.25) * mm});
            skSolve(sketch);
        }
        {
            var Q0;
            {var subQ1=sQuery(id+"F31.wireOp",EDGE,"E111");Q0=makeQuery(id+"F31.imprint","IMPRINT",FACE,{"disambiguationData":[TD([[makeQuery(id+"F31.imprint","IMPRINT",EDGE,{"derivedFrom":subQ1}),-1.0]])]});}
            var Q1;
            {var subQ3=sQuery(id+"F31.wireOp",EDGE,"E105");Q1=makeQuery(id+"F31.imprint","IMPRINT",FACE,{"disambiguationData":[TD([[makeQuery(id+"F31.imprint","IMPRINT",EDGE,{"derivedFrom":subQ3}),-1.0]])]});}
            var Q2;
            {var subQ0=sQuery(id+"F31.wireOp",EDGE,"E114.MirrorCS");Q2=makeQuery(id+"F31.imprint","IMPRINT",FACE,{"disambiguationData":[TD([[makeQuery(id+"F31.imprint","IMPRINT",EDGE,{"derivedFrom":subQ0}),1.0]])]});}
            var Q3;
            Q3=makeQuery(id+"F20.boolean.opBoolean","COPY",FACE,{"derivedFrom":makeQuery(id+"F20.opExtrude","CAP_FACE",FACE,{"disambiguationData":[OSD([sQuery(id+"F19.wireOp",EDGE,"E30.bottom"),sQuery(id+"F19.wireOp",EDGE,"E30.top"),sQuery(id+"F19.wireOp",EDGE,"E30.left"),sQuery(id+"F19.wireOp",EDGE,"E30.right")])],"isStart":false})});
            extrude(context, id + "F32", {"entities" : qUnion([Q0, Q1, Q2]), "operationType" : NewBodyOperationType.REMOVE, "endBound" : BoundingType.UP_TO_SURFACE, "oppositeDirection" : true, "endBoundEntityFace" : qUnion([Q3]), "depth" : 25.4 * mm});
        }
        {
            var Q0;
            {var subQ3=sQuery(id+"F31.wireOp",EDGE,"E105");Q0=makeQuery(id+"F31.imprint","IMPRINT",FACE,{"disambiguationData":[TD([[makeQuery(id+"F31.imprint","IMPRINT",EDGE,{"derivedFrom":subQ3}),1.0]])]});}
            var Q1;
            {var subQ0=sQuery(id+"F31.wireOp",EDGE,"E114.MirrorCS");Q1=makeQuery(id+"F31.imprint","IMPRINT",FACE,{"disambiguationData":[TD([[makeQuery(id+"F31.imprint","IMPRINT",EDGE,{"derivedFrom":subQ0}),-1.0]])]});}
            extrude(context, id + "F33", {"entities" : qUnion([Q0, Q1]), "operationType" : NewBodyOperationType.REMOVE, "oppositeDirection" : true, "depth" : 2.25 * mm});
        }
        {
            var Q0;
            {var subQ3=sQuery(id+"F31.wireOp",EDGE,"E108");Q0=makeQuery(id+"F31.imprint","IMPRINT",FACE,{"disambiguationData":[TD([[makeQuery(id+"F31.imprint","IMPRINT",EDGE,{"derivedFrom":subQ3}),1.0]])]});}
            var Q1;
            {var subQ4=sQuery(id+"F31.wireOp",EDGE,"E118.MirrorCS");Q1=makeQuery(id+"F31.imprint","IMPRINT",FACE,{"disambiguationData":[TD([[makeQuery(id+"F31.imprint","IMPRINT",EDGE,{"derivedFrom":subQ4}),-1.0]])]});}
            extrude(context, id + "F34", {"entities" : qUnion([Q0, Q1]), "operationType" : NewBodyOperationType.REMOVE, "oppositeDirection" : true, "depth" : 3 * mm});
        }
        {
            var Q0;
            Q0=makeQuery(id+"F16.opExtrude","SWEPT_FACE",FACE,{"disambiguationData":[OSD([sQuery(id+"F15.wireOp",EDGE,"E26.right")])]});
            var sketch = newSketch(context, id + "F35", { "sketchPlane" : qUnion([Q0])});
            skLineSegment(sketch, "E121", {"start": v(2.45, 7) * mm, "end": v(2.45, 5) * mm});
            skLineSegment(sketch, "E122", {"start": v(2.45, 5) * mm, "end": v(0.7, 4) * mm});
            skSolve(sketch);
        }
        {
            var Q0;
            {var subQ0=sQuery(id+"F35.wireOp",EDGE,"E121");Q0=makeQuery(id+"F35.imprint","IMPRINT",FACE,{"disambiguationData":[TD([[makeQuery(id+"F35.imprint","IMPRINT",EDGE,{"derivedFrom":subQ0}),-1.0]])]});}
            extrude(context, id + "F36", {"entities" : qUnion([Q0]), "operationType" : NewBodyOperationType.REMOVE, "endBound" : BoundingType.THROUGH_ALL, "oppositeDirection" : true, "depth" : 25.4 * mm});
        }
        {
            var Q0;
            {var subQ0=sQuery(id+"F19.wireOp",EDGE,"E30.right");var subQ1=sQuery(id+"F19.wireOp",EDGE,"E30.left");var subQ2=sQuery(id+"F19.wireOp",EDGE,"E30.top");var subQ3=sQuery(id+"F19.wireOp",EDGE,"E30.bottom");Q0=makeQuery(id+"F32.boolean.opBoolean","MERGE",FACE,{"derivedFrom":[makeQuery(id+"F20.boolean.opBoolean","COPY",FACE,{"derivedFrom":makeQuery(id+"F20.opExtrude","CAP_FACE",FACE,{"disambiguationData":[OSD([subQ3,subQ2,subQ1,subQ0])],"isStart":false})}),makeQuery(id+"F32.opExtrude","CAP_FACE",FACE,{"disambiguationData":[OSD([subQ3,subQ2,subQ1,subQ0]),ownerDisambiguation([makeQuery(id+"F31.imprint","IMPRINT",EDGE,{"derivedFrom":sQuery(id+"F31.wireOp",EDGE,"E111")})])],"isStart":false})]});}
            var sketch = newSketch(context, id + "F37", { "sketchPlane" : qUnion([Q0])});
            skLineSegment(sketch, "E123", {"start": v(-15.65, 6.37) * mm, "end": v(-15.65, 2.37) * mm, "construction": true});
            skLineSegment(sketch, "E124.bottom", {"start": v(-16.53, 4.62) * mm, "end": v(-16.78, 4.62) * mm});
            skLineSegment(sketch, "E124.top", {"start": v(-16.53, 4.87) * mm, "end": v(-16.78, 4.87) * mm});
            skLineSegment(sketch, "E124.left", {"start": v(-16.53, 4.62) * mm, "end": v(-16.53, 4.87) * mm});
            skLineSegment(sketch, "E124.right", {"start": v(-16.78, 4.62) * mm, "end": v(-16.78, 4.87) * mm});
            skPoint(sketch, "E124.middle", {"position": v(-16.65, 4.75) * mm});
            skPoint(sketch, "E125.MirrorP", {"position": v(-14.65, 4.75) * mm});
            skLineSegment(sketch, "E126.MirrorCS", {"start": v(-14.78, 4.87) * mm, "end": v(-14.53, 4.87) * mm});
            skLineSegment(sketch, "E127.MirrorCS", {"start": v(-14.78, 4.62) * mm, "end": v(-14.53, 4.62) * mm});
            skLineSegment(sketch, "E128.MirrorCS", {"start": v(-14.53, 4.62) * mm, "end": v(-14.53, 4.87) * mm});
            skLineSegment(sketch, "E129.MirrorCS", {"start": v(-14.78, 4.62) * mm, "end": v(-14.78, 4.87) * mm});
            skSolve(sketch);
        }
        {
            var Q0;
            Q0=qSketchRegion(id+"F37",true);
            var Q1;
            Q1=makeQuery(id+"F33.boolean.opBoolean","COPY",FACE,{"derivedFrom":makeQuery(id+"F33.opExtrude","CAP_FACE",FACE,{"disambiguationData":[OSD([sQuery(id+"F19.wireOp",EDGE,"E30.right"),sQuery(id+"F31.wireOp",EDGE,"E104"),sQuery(id+"F31.wireOp",EDGE,"E105"),sQuery(id+"F31.wireOp",EDGE,"E106")])],"isStart":false})});
            extrude(context, id + "F38", {"entities" : qUnion([Q0]), "endBoundEntityFace" : qUnion([Q1]), "depth" : 4 * mm});
        }
    });
